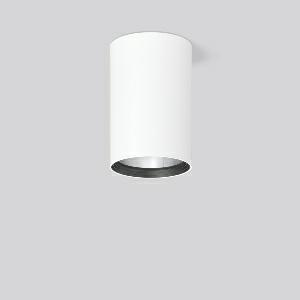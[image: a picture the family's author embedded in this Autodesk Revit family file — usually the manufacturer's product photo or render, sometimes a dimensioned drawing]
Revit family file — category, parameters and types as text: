
# Revit family: heledon_maxi_a_931219_002_3_26f9
name_source: partatom
category: Lighting Fixtures
units: mm (PartAtom-declared; Revit-internal decimal feet)

## family parameters
Cut with Voids When Loaded = No
Host = Face
Light Source = No
Part Type = Normal
Room Calculation Point = No
Round Connector Dimension = Use Diameter
Shared = No

## types (1)
- HELEDON maxi A (1 x LED Modul 935, 3250 lm, 3500)
    Apparent Load = 25 VA
    Approval mark = CE
    CIE Flux Codes = 97 100 100 100 100
    Color Rendering = 92
    Color Temperature = 3500
    Default Elevation = 1800 mm
    Description = Series: HELEDON maxi
Cylindrical surface-mounted downlight. Housing: die-cast aluminium, powder-coated. Internal ceiling frame polycarbonate with bayonet mounting. Black plastic ring and recessed LED to prevent glare from the side. Optical assembly with reflector made of MIRO-Silver with 98% total light reflection for outstanding efficiency - can be changed without tools. Best colour rendering index Ra>90. Suitable for Ceiling mounting. Easy installation with a separate ceiling frame with bayonet mounting and plug connection. Driver integrated. Connected via plug-in connector. High quality converter without flickering and stroboscopic effect. The following accessories can be mounted without use of tools: interchangeable lenses, decorative glasses, honeycomb louvre, clear and frosted diffusers, white interchangeable plastic ring. 
Colour: traffic white, matt (RAL 9016)
Diameter: 123 mm
Height: 183 mm
Lamp: LED
Socket: without socket
Colour temperature: 3500K
Colour rendering index (CRI): 92
System power: 25 W
Rated luminous flux: 3250 lm
Luminous efficiency: 130 lm/W
Control gear: Regulated power supply
Protection class: I
Type of protection: IP 20
    Height = 183 mm
    Lamp = 1 x LED Modul 935
    Lamp Light Flux = 3250 lm
    Lamp count = 1
    Length = 123 mm
    Lifetime = 50000 h
    Luminous efficacy = 130 lm/W
    Manufacturer = RZB
    ModVariant = No
    Model = 931219.002.3
    Mounting Place = Ceiling
    Mounting Type = Surface mounted
    Number of Poles = 1
    OnlyDefault = Yes
    Power Factor = 1
    Product Name = HELEDON maxi A
    Product group = Surface mounted downlights
    ProductGroupID = 302
    Protection Class = Protection class I
    Protection Degree = IP 20
    RLX_Detail_Level = 1
    RLX_Emergency_Light_Flux = 0 lm
    RLX_Emergency_Type = 0
    RLX_Emergency_Type_DB = No
    RlxData = <blob elided: 98093 chars, md5=759a68f4>
    Socket = socket
    Standby Power = 0 W
    System Light Flux = 3250 lm
    System Power = 25 W
    Type Comments = Product without accessories
    Type Image = 931192.002.jpg
    URL = http://relux.com
    VarID = ---
    Voltage = 230 V
    Voltage Range = 220-240 V
    Weight = 0.00 kg
    Width = 0 mm  [stored 0 ft]

note: [stored X ft] marks values corroborated as IEEE doubles in the binary element streams (Revit-internal decimal feet)

## geometry (parser evidence)
native form markers: Blend x4, Sweep x12
no freeform markers — native parametric forms only
